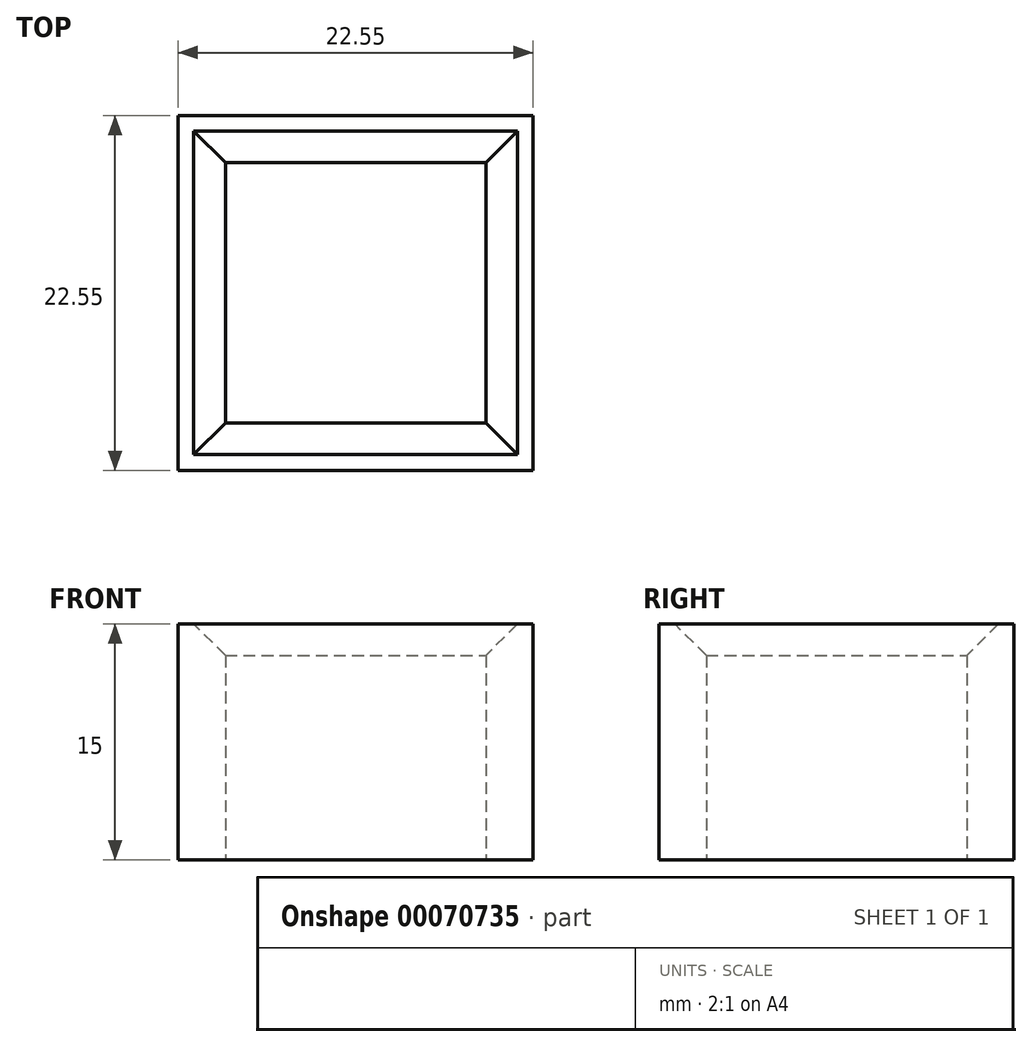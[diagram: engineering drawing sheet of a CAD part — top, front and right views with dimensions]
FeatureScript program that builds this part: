
annotation { "Feature Type Name" : "Feature", "Feature Type Description" : "" }
export const myFeature = defineFeature(function(context is Context, id is Id, definition is map)
    precondition{}
    {
        {
            var Q0;
            Q0=qCreatedBy(makeId("Top.planeOp"),FACE);
            var sketch = newSketch(context, id + "F0", { "sketchPlane" : qUnion([Q0])});
            skLineSegment(sketch, "E0.bottom", {"start": v(0, 0) * mm, "end": v(-16.55, 0) * mm});
            skLineSegment(sketch, "E0.top", {"start": v(0, 16.55) * mm, "end": v(-16.55, 16.55) * mm});
            skLineSegment(sketch, "E0.left", {"start": v(0, 0) * mm, "end": v(0, 16.55) * mm});
            skLineSegment(sketch, "E0.right", {"start": v(-16.55, 0) * mm, "end": v(-16.55, 16.55) * mm});
            skLineSegment(sketch, "E1.0", {"start": v(3, -3) * mm, "end": v(-19.55, -3) * mm});
            skLineSegment(sketch, "E1.1", {"start": v(3, -3) * mm, "end": v(3, 19.55) * mm});
            skLineSegment(sketch, "E1.2", {"start": v(3, 19.55) * mm, "end": v(-19.55, 19.55) * mm});
            skLineSegment(sketch, "E1.3", {"start": v(-19.55, -3) * mm, "end": v(-19.55, 19.55) * mm});
            skSolve(sketch);
        }
        {
            var Q0;
            Q0 = qSketchRegion(id + "F0", true);
            extrude(context, id + "F1", {"entities" : qUnion([Q0]), "depth" : 5 * mm});
        }
        {
            var Q0;
            Q0 = qSketchRegion(id + "F0", true);
            extrude(context, id + "F2", {"entities" : qUnion([Q0]), "operationType" : NewBodyOperationType.ADD, "depth" : 15 * mm});
        }
        {
            var Q0;
            Q0=makeQuery(id+"F2.opExtrude","CAP_EDGE",EDGE,{"disambiguationData":[OSD([sQuery(id+"F0.wireOp",EDGE,"E0.top")])],"isStart":false});
            var Q1;
            Q1=makeQuery(id+"F2.opExtrude","CAP_EDGE",EDGE,{"disambiguationData":[OSD([sQuery(id+"F0.wireOp",EDGE,"E0.right")])],"isStart":false});
            var Q2;
            Q2=makeQuery(id+"F2.opExtrude","CAP_EDGE",EDGE,{"disambiguationData":[OSD([sQuery(id+"F0.wireOp",EDGE,"E0.left")])],"isStart":false});
            var Q3;
            Q3=makeQuery(id+"F2.opExtrude","CAP_EDGE",EDGE,{"disambiguationData":[OSD([sQuery(id+"F0.wireOp",EDGE,"E0.bottom")])],"isStart":false});
            chamfer(context, id + "F3", {"entities" : qUnion([Q0, Q1, Q2, Q3]), "width" : 2 * mm, "tangentPropagation" : true});
        }
    });
